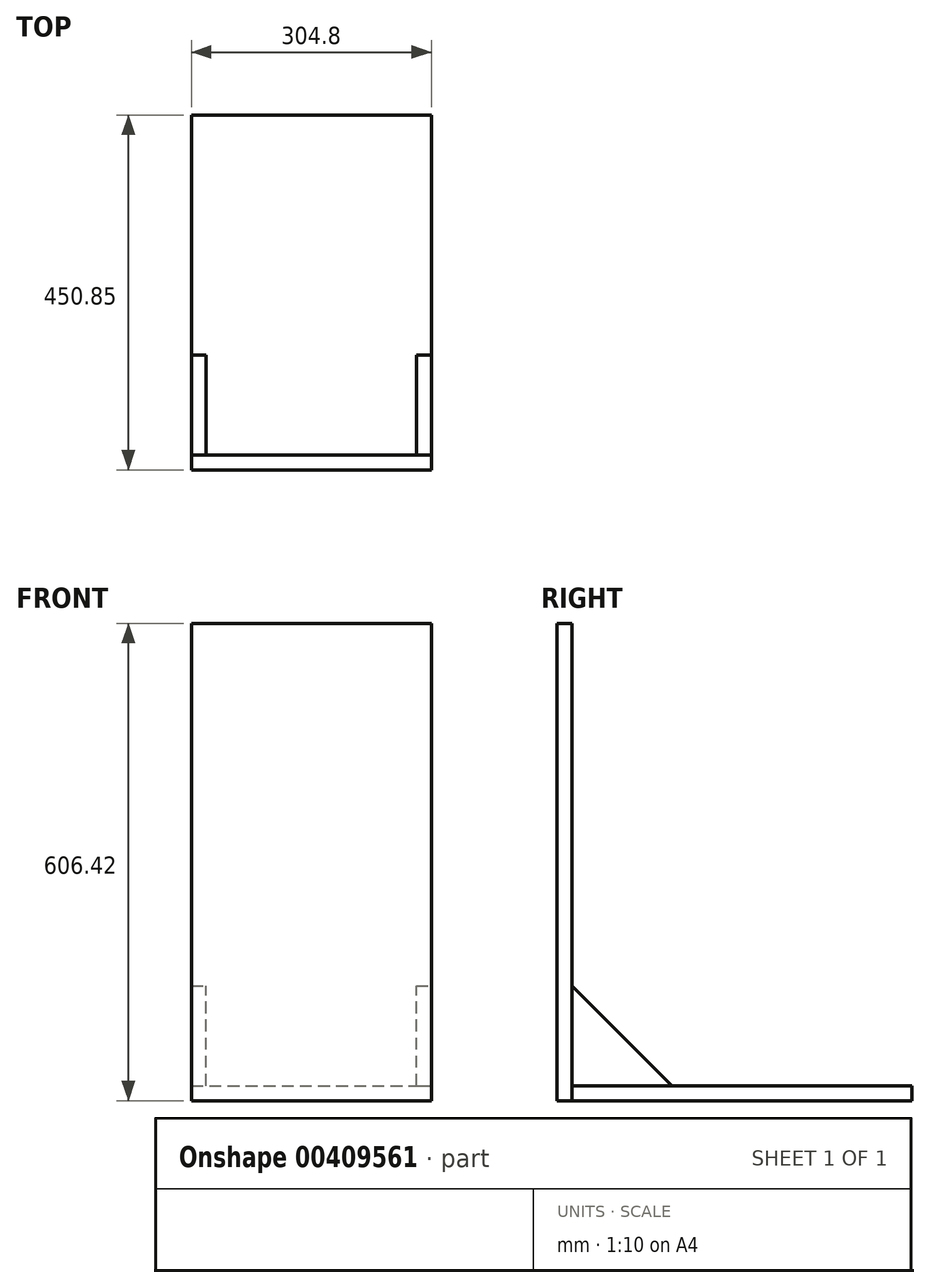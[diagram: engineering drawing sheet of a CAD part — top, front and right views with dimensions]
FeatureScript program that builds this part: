
annotation { "Feature Type Name" : "Feature", "Feature Type Description" : "" }
export const myFeature = defineFeature(function(context is Context, id is Id, definition is map)
    precondition{}
    {
        {
            var Q0;
            Q0=qCreatedBy(makeId("Top.planeOp"),FACE);
            var sketch = newSketch(context, id + "F0", { "sketchPlane" : qUnion([Q0])});
            skLineSegment(sketch, "E0.bottom", {"start": v(-152.4, 0) * mm, "end": v(152.4, 0) * mm});
            skLineSegment(sketch, "E0.top", {"start": v(-152.4, 431.8) * mm, "end": v(152.4, 431.8) * mm});
            skLineSegment(sketch, "E0.left", {"start": v(-152.4, 0) * mm, "end": v(-152.4, 431.8) * mm});
            skLineSegment(sketch, "E0.right", {"start": v(152.4, 0) * mm, "end": v(152.4, 431.8) * mm});
            skSolve(sketch);
        }
        {
            var Q0;
            Q0 = qSketchRegion(id + "F0", true);
            extrude(context, id + "F1", {"entities" : qUnion([Q0]), "depth" : 19.05 * mm});
        }
        {
            var Q0;
            Q0=qCreatedBy(makeId("Front.planeOp"),FACE);
            var sketch = newSketch(context, id + "F2", { "sketchPlane" : qUnion([Q0])});
            skLineSegment(sketch, "E1.bottom", {"start": v(-152.4, 0) * mm, "end": v(152.4, 0) * mm});
            skLineSegment(sketch, "E1.top", {"start": v(-152.4, 606.43) * mm, "end": v(152.4, 606.43) * mm});
            skLineSegment(sketch, "E1.left", {"start": v(-152.4, 0) * mm, "end": v(-152.4, 606.43) * mm});
            skLineSegment(sketch, "E1.right", {"start": v(152.4, 0) * mm, "end": v(152.4, 606.43) * mm});
            skSolve(sketch);
        }
        {
            var Q0;
            Q0 = qSketchRegion(id + "F2", true);
            extrude(context, id + "F3", {"entities" : qUnion([Q0]), "depth" : 19.05 * mm});
        }
        {
            var Q0;
            Q0=makeQuery(id+"F3.opExtrude","SWEPT_FACE",FACE,{"disambiguationData":[OSD([sQuery(id+"F2.wireOp",EDGE,"E1.right")])]});
            var sketch = newSketch(context, id + "F4", { "sketchPlane" : qUnion([Q0])});
            skLineSegment(sketch, "E2", {"start": v(0, 19.05) * mm, "end": v(0, 146.05) * mm});
            skLineSegment(sketch, "E3", {"start": v(0, 146.05) * mm, "end": v(0, 146.05) * mm});
            skLineSegment(sketch, "E4", {"start": v(127, 19.05) * mm, "end": v(0, 146.05) * mm});
            skLineSegment(sketch, "E5", {"start": v(0, 19.05) * mm, "end": v(127, 19.05) * mm});
            skSolve(sketch);
        }
        {
            var Q0;
            Q0 = qSketchRegion(id + "F4", true);
            extrude(context, id + "F5", {"entities" : qUnion([Q0]), "oppositeDirection" : true, "depth" : 19.05 * mm});
        }
        {
            var Q0;
            Q0=makeQuery(id+"F5.opExtrude","SWEPT_BODY",BODY,{"disambiguationData":[OSD([sQuery(id+"F4.wireOp",EDGE,"E2"),sQuery(id+"F4.wireOp",EDGE,"E4"),sQuery(id+"F4.wireOp",EDGE,"E5")])]});
            var Q1;
            Q1=makeQuery(id+"F1.opExtrude","CAP_EDGE",EDGE,{"disambiguationData":[OSD([sQuery(id+"F0.wireOp",EDGE,"E0.top")])],"isStart":false});
            transform(context, id + "F6", {"entities" : qUnion([Q0]), "transformType" : TransformType.TRANSLATION_DISTANCE, "transformDirection" : qUnion([Q1]), "distance" : 285.75 * mm, "oppositeDirection" : true, "makeCopy" : true});
        }
    });
